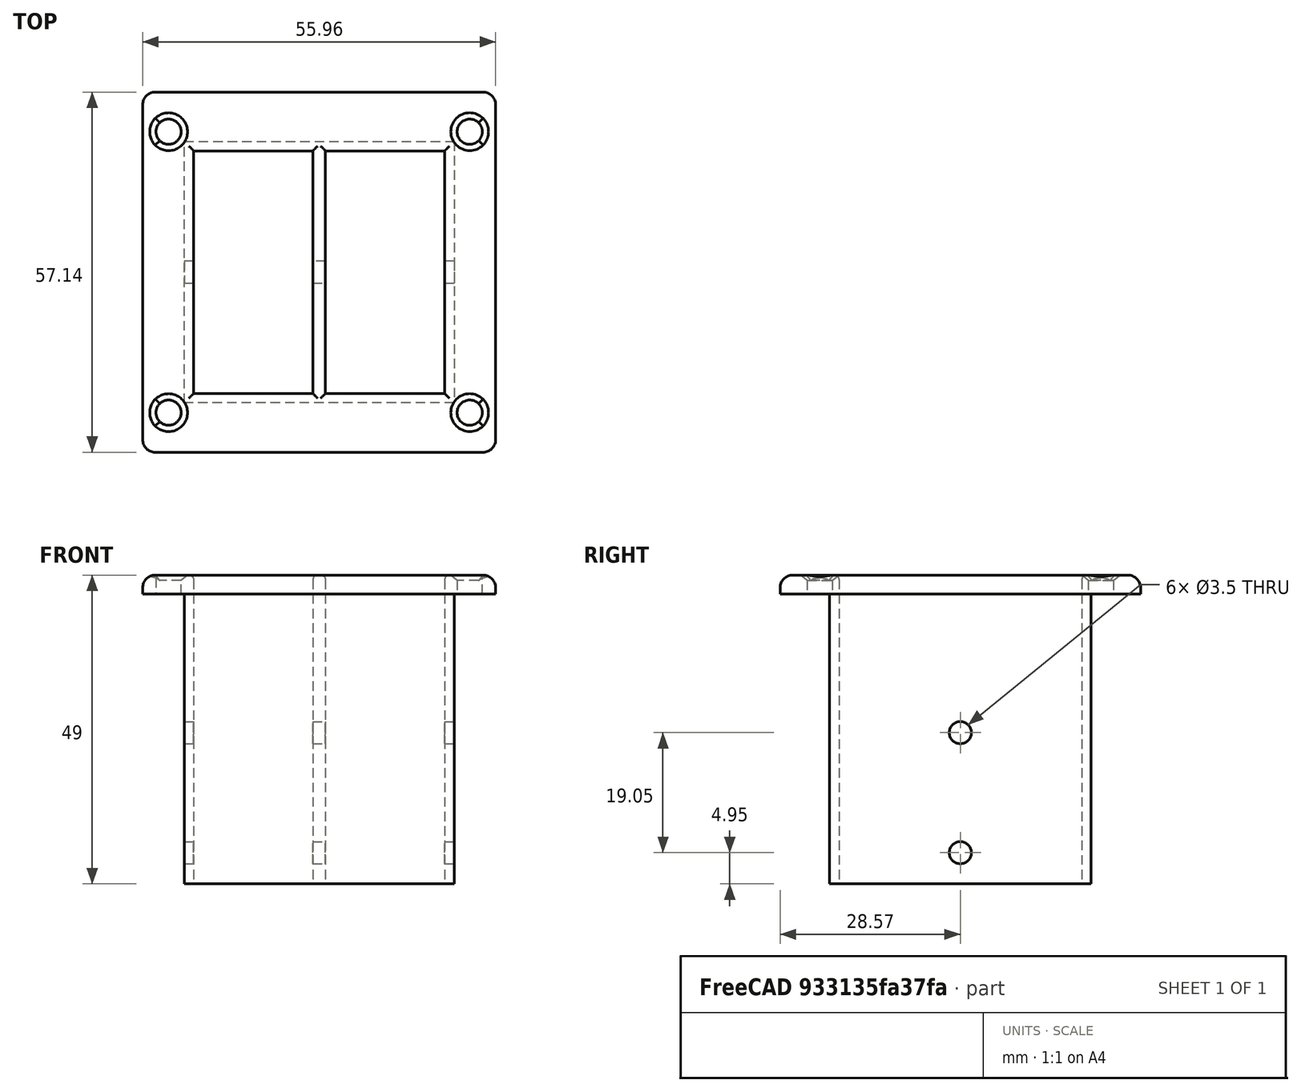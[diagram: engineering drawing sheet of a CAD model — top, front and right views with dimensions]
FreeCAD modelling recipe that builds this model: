
FCSTD DOCUMENT  (FreeCAD 0.19R24291 (Git))
Label: PanelPlate_SB
License: All rights reserved
LicenseURL: http://en.wikipedia.org/wiki/All_rights_reserved
objects: TechDraw::DrawViewDimension×33, Sketcher::SketchObject×10, TechDraw::DrawProjGroupItem×8, PartDesign::Fillet×7, PartDesign::Pocket×6, PartDesign::Pad×4, Spreadsheet::Sheet×2, TechDraw::DrawSVGTemplate×2, PartDesign::Chamfer×2, PartDesign::Body×2, TechDraw::DrawProjGroup×2, TechDraw::DrawPage×2, App::Part×2
note: 50 computed .brp shape members not serialized (recipe doc carries the construction recipe); baked Part::Feature solids carry a one-line shape summary decoded from their .brp

FEATURE [Sketcher::SketchObject] Sketch
  FullyConstrained = true
  MapMode = 5
  Support = -> [XY_Plane001]
  expr: Constraints[10] = <<Spreadsheet_PanelPlate_SB>>.SB1_FacePlateHeight
  expr: Constraints[9] = <<Spreadsheet_PanelPlate_SB>>.SB1_FacePlateWidth
  sketch-geometry (4):
    g0: LineSegment StartX=-19.05 StartY=28.575 StartZ=0 EndX=19.05 EndY=28.575 EndZ=0
    g1: LineSegment StartX=19.05 StartY=28.575 StartZ=0 EndX=19.05 EndY=-28.575 EndZ=0
    g2: LineSegment StartX=19.05 StartY=-28.575 StartZ=0 EndX=-19.05 EndY=-28.575 EndZ=0
    g3: LineSegment StartX=-19.05 StartY=-28.575 StartZ=0 EndX=-19.05 EndY=28.575 EndZ=0
  constraints (11):
    c: Coincident(g0,g1)
    c: Coincident(g1,g2)
    c: Coincident(g2,g3)
    c: Coincident(g3,g0)
    c: Horizontal(g0)
    c: Horizontal(g2)
    c: Vertical(g1)
    c: Vertical(g3)
    c: Symmetric(g0,g1,g-1)
    c: DistanceX(g0,g0) = 38.1
    c: DistanceY(g1,g1) = 57.15
FEATURE [Spreadsheet::Sheet] Spreadsheet  label="Spreadsheet_PanelPlate_SB"
  cells = A1=Panel Plate SB connector; C1=AndersonDept; D1(AndersonDept)==49mm; E1=Given; F1=Anderson_Screw_Ofset; G1(Anderson_Screw_Ofset)==23mm; A2=Based on Powerwerx; C2=AndersonWidth; D2(AndersonWidth)==15.9mm; E2=Given; F2=Anderson_Screw_Space; G2(Anderson_Screw_Space)==25.4 * 0.75mm; A3=Anderson is 37x15.9x49 mm; C3=AndersonHeight; D3(AndersonHeight)==37mm; E3=Given; F3=Anderson_Screw_Hole; G3(Anderson_Screw_Hole)==3.5mm; H3=Measured; A7=One up Panel Plate; D7=Inch; F7=Two up Panel Plate; A8=SB1_FacePlateWidth; B8(SB1_FacePlateWidth)==D8; C8=Guestamet from photo; D8==1.5in; F8=SB2_FacePlateWidth; G8(SB2_FacePlateWidth)==G9 * 2.914 / 2.976; A9=SB1_FacePlateHeight; B9(SB1_FacePlateHeight)==D9; C9=Guestamet from photo; D9==2.25in; F9=SB2_FacePlateHeight; G9(SB2_FacePlateHeight)==B9; A10=SB1_MtgHole_Width; B10(SB1_MtgHole_Width)==D10; C10=From Powerwerx; D10==1.02in; F10=SB2_MtgHole_Width; G10(SB2_MtgHole_Width)==1.88in; A11=SB1_MtgHole_Height; B11(SB1_MtgHole_Height)==D11; C11=From Powerwerx; D11==1.755in; F11=SB2_MtgHole_Height; G11(SB2_MtgHole_Height)==B11; A12=SB1_MtgHole_Diameter; B12(SB1_MtgHole_Diameter)==4mm; C12=Standardizing; F12=SB2_MtgHole_Diameter; G12(SB2_MtgHole_Diameter)==B12; A13=SB1_Thickness; B13(SB1_Thickness)==3mm; C13=Guess; F13=SB2_Thickness; G13(SB2_Thickness)==B13; A15=SB1_ExtrusionWidth; B15(SB1_ExtrusionWidth)==D2 + 2 * E15; D15=Add 2.5mm to Anderson; E15==2.25mm; F15=SB2_ExtrusionWidth; G15(SB2_ExtrusionWidth)==B15 + B15 + G19; H15=wrong; A16=SB1_ExtrusionHeight; B16(SB1_ExtrusionHeight)==D3 + 2 * E15; F16=SB2_ExtrusionHeight; G16(SB2_ExtrusionHeight)==B16; A17=SB1_ExtrusionDepth; B17(SB1_ExtrusionDepth)==D1; F17=SB2_ExtrusionDepth; G17(SB2_ExtrusionDepth)==B17; A18=SB1_ExtrusionWallThick; B18(SB1_ExtrusionWallThick)==1.5mm; F18=SB2_ExtrusionWallThick; G18(SB2_ExtrusionWallThick)==B18; F19=SB2_ExtrusionDividerThick; G19(SB2_ExtrusionDividerThick)==2mm; H19=guess
FEATURE [PartDesign::Pad] Pad  label="PadFaceplateSB1"
  Direction = (1,1,1)
  Length = 3
  Length2 = 100
  Profile = -> Sketch
  Type = 0
  expr: Length = <<Spreadsheet_PanelPlate_SB>>.SB1_Thickness
FEATURE [Sketcher::SketchObject] Sketch001
  FullyConstrained = true
  MapMode = 5
  Support = -> [XY_Plane001]
  expr: Constraints[9] = <<Spreadsheet_PanelPlate_SB>>.SB1_MtgHole_Height
  expr: Constraints[8] = <<Spreadsheet_PanelPlate_SB>>.SB1_MtgHole_Width
  expr: Constraints[0] = <<Spreadsheet_PanelPlate_SB>>.SB1_MtgHole_Diameter
  sketch-geometry (4):
    g0: Circle CenterX=-12.954 CenterY=22.2885 CenterZ=0 NormalX=0 NormalY=0 NormalZ=1 AngleXU=0 Radius=2
    g1: Circle CenterX=-12.954 CenterY=-22.2885 CenterZ=0 NormalX=0 NormalY=0 NormalZ=1 AngleXU=0 Radius=2
    g2: Circle CenterX=12.954 CenterY=22.2885 CenterZ=0 NormalX=0 NormalY=0 NormalZ=1 AngleXU=0 Radius=2
    g3: Circle CenterX=12.954 CenterY=-22.2885 CenterZ=0 NormalX=0 NormalY=0 NormalZ=1 AngleXU=0 Radius=2
  constraints (11):
    c: Diameter(g0) = 4
    c: Equal(g0,g2)
    c: Equal(g2,g3)
    c: Equal(g3,g1)
    c: Horizontal(g0,g2)
    c: Horizontal(g1,g3)
    c: Vertical(g0,g1)
    c: Vertical(g2,g3)
    c: DistanceX(g0,g2) = 25.908
    c: DistanceY(g3,g2) = 44.577
    c: Symmetric(g0,g3,g-1)
FEATURE [PartDesign::Pocket] Pocket  label="PocketMtgHolesSB1"
  BaseFeature = -> Pad
  Length = 5
  Length2 = 100
  Profile = -> Sketch001
  Reversed = true
  Type = 1
FEATURE [Sketcher::SketchObject] Sketch002
  AttachmentOffset = pos=(0,0,3) rot=(0,0,1;0rad)
  FullyConstrained = true
  MapMode = 5
  Placement = pos=(0,0,3) rot=(0,0,1;0rad)
  Support = -> [XY_Plane001]
  expr: Constraints[10] = <<Spreadsheet_PanelPlate_SB>>.SB1_ExtrusionHeight
  expr: Constraints[20] = Spreadsheet.AndersonWidth
  expr: Constraints[21] = <<Spreadsheet_PanelPlate_SB>>.AndersonHeight
  expr: Constraints[9] = <<Spreadsheet_PanelPlate_SB>>.SB1_ExtrusionWidth
  expr: .AttachmentOffset.Base.z = <<Spreadsheet_PanelPlate_SB>>.SB1_Thickness
  sketch-geometry (8):
    g0: LineSegment StartX=-10.2 StartY=20.75 StartZ=0 EndX=10.2 EndY=20.75 EndZ=0
    g1: LineSegment StartX=10.2 StartY=20.75 StartZ=0 EndX=10.2 EndY=-20.75 EndZ=0
    g2: LineSegment StartX=10.2 StartY=-20.75 StartZ=0 EndX=-10.2 EndY=-20.75 EndZ=0
    g3: LineSegment StartX=-10.2 StartY=-20.75 StartZ=0 EndX=-10.2 EndY=20.75 EndZ=0
    g4: LineSegment StartX=-7.95 StartY=18.5 StartZ=0 EndX=7.95 EndY=18.5 EndZ=0
    g5: LineSegment StartX=7.95 StartY=18.5 StartZ=0 EndX=7.95 EndY=-18.5 EndZ=0
    g6: LineSegment StartX=7.95 StartY=-18.5 StartZ=0 EndX=-7.95 EndY=-18.5 EndZ=0
    g7: LineSegment StartX=-7.95 StartY=-18.5 StartZ=0 EndX=-7.95 EndY=18.5 EndZ=0
  constraints (22):
    c: Coincident(g0,g1)
    c: Coincident(g1,g2)
    c: Coincident(g2,g3)
    c: Coincident(g3,g0)
    c: Horizontal(g0)
    c: Horizontal(g2)
    c: Vertical(g1)
    c: Vertical(g3)
    c: Symmetric(g0,g1,g-1)
    c: DistanceX(g0,g0) = 20.4
    c: DistanceY(g3,g3) = 41.5
    c: Coincident(g4,g5)
    c: Coincident(g5,g6)
    c: Coincident(g6,g7)
    c: Coincident(g7,g4)
    c: Horizontal(g4)
    c: Horizontal(g6)
    c: Vertical(g5)
    c: Vertical(g7)
    c: Symmetric(g4,g5,g-1)
    c: DistanceX(g4,g4) = 15.9
    c: DistanceY(g5,g5) = 37
FEATURE [PartDesign::Pad] Pad001  label="PadExtrusionBodyDownSB1"
  BaseFeature = -> Pocket
  Direction = (1,1,1)
  Length = 49
  Length2 = 100
  Profile = -> Sketch002
  Refine = true
  Reversed = true
  Type = 0
  expr: Length = <<Spreadsheet_PanelPlate_SB>>.SB1_ExtrusionDepth
FEATURE [Sketcher::SketchObject] Sketch003
  FullyConstrained = true
  MapMode = 5
  Placement = pos=(0,0,3) rot=(0,0,1;0rad)
  Support = -> [Pad001]
  expr: Constraints[9] = <<Spreadsheet_PanelPlate_SB>>.SB1_ExtrusionHeight - 2 * Spreadsheet.SB1_ExtrusionWallThick
  expr: Constraints[10] = <<Spreadsheet_PanelPlate_SB>>.SB1_ExtrusionWidth - 2 * Spreadsheet.SB1_ExtrusionWallThick
  expr: Constraints[20] = <<Spreadsheet_PanelPlate_SB>>.AndersonWidth
  expr: Constraints[21] = <<Spreadsheet_PanelPlate_SB>>.AndersonHeight
  sketch-geometry (8):
    g0: LineSegment StartX=-8.7 StartY=19.25 StartZ=0 EndX=8.7 EndY=19.25 EndZ=0
    g1: LineSegment StartX=8.7 StartY=19.25 StartZ=0 EndX=8.7 EndY=-19.25 EndZ=0
    g2: LineSegment StartX=8.7 StartY=-19.25 StartZ=0 EndX=-8.7 EndY=-19.25 EndZ=0
    g3: LineSegment StartX=-8.7 StartY=-19.25 StartZ=0 EndX=-8.7 EndY=19.25 EndZ=0
    g4: LineSegment StartX=-7.95 StartY=18.5 StartZ=0 EndX=7.95 EndY=18.5 EndZ=0
    g5: LineSegment StartX=7.95 StartY=18.5 StartZ=0 EndX=7.95 EndY=-18.5 EndZ=0
    g6: LineSegment StartX=7.95 StartY=-18.5 StartZ=0 EndX=-7.95 EndY=-18.5 EndZ=0
    g7: LineSegment StartX=-7.95 StartY=-18.5 StartZ=0 EndX=-7.95 EndY=18.5 EndZ=0
  constraints (22):
    c: Coincident(g0,g1)
    c: Coincident(g1,g2)
    c: Coincident(g2,g3)
    c: Coincident(g3,g0)
    c: Horizontal(g0)
    c: Horizontal(g2)
    c: Vertical(g1)
    c: Vertical(g3)
    c: Symmetric(g0,g1,g-1)
    c: DistanceY(g1,g1) = 38.5
    c: DistanceX(g0,g0) = 17.4
    c: Coincident(g4,g5)
    c: Coincident(g5,g6)
    c: Coincident(g6,g7)
    c: Coincident(g7,g4)
    c: Horizontal(g4)
    c: Horizontal(g6)
    c: Vertical(g5)
    c: Vertical(g7)
    c: Symmetric(g4,g5,g-1)
    c: DistanceX(g4,g4) = 15.9
    c: DistanceY(g5,g5) = 37
FEATURE [TechDraw::DrawSVGTemplate] Template
  EditableTexts = Approved1=Approved 1; Approved2=Approved 2; CheckedBy=20230810; Code=Code; CompanyAddress=publicinvention.org; CompanyName=Public Invention; DrawingNumber=Drawing Number; DrawingTitle1=PanelPlate SB1; DrawingTitle2=For Anderson SB50 Connectors; DrawingTitle3=Drawing Title 3; DrawnBy=(Forrest) Lee Erickson; Revision=Rev; Scale=Scale; Sheet=Sheet 1 of 1
  Height = 215.9
  Orientation = 1
  Width = 279.4
FEATURE [PartDesign::Pocket] Pocket001  label="PocketThroughBodySB1"
  BaseFeature = -> Pad001
  Length = 5
  Length2 = 100
  Profile = -> Sketch003
  Type = 1
FEATURE [Sketcher::SketchObject] Sketch004
  FullyConstrained = true
  MapMode = 5
  Placement = pos=(10.2,0,0) rot=(0.57735,0.57735,0.57735;2.0944rad)
  Support = -> [Pocket001]
  expr: Constraints[2] = <<Spreadsheet_PanelPlate_SB>>.Anderson_Screw_Hole
  expr: Constraints[5] = <<Spreadsheet_PanelPlate_SB>>.Anderson_Screw_Space
  expr: Constraints[4] = Spreadsheet.Anderson_Screw_Ofset - <<Spreadsheet_PanelPlate_SB>>.SB1_Thickness
  sketch-geometry (2):
    g0: Circle CenterX=0 CenterY=-20 CenterZ=0 NormalX=0 NormalY=0 NormalZ=1 AngleXU=0 Radius=1.75
    g1: Circle CenterX=0 CenterY=-39.05 CenterZ=0 NormalX=0 NormalY=0 NormalZ=1 AngleXU=0 Radius=1.75
  constraints (6):
    c: PointOnObject(g0,g-2)
    c: PointOnObject(g1,g-2)
    c: Diameter(g0) = 3.5
    c: Equal(g0,g1)
    c: DistanceY(g0,g-1) = 20
    c: DistanceY(g1,g0) = 19.05
FEATURE [PartDesign::Pocket] Pocket002  label="PocketMoutScrewsSB1"
  BaseFeature = -> Pocket001
  Length = 5
  Length2 = 100
  Profile = -> Sketch004
  Type = 1
FEATURE [PartDesign::Chamfer] Chamfer
  Angle = 41
  Base = -> Pocket002 [Edge28,Edge23,Edge21,Edge22]
  BaseFeature = -> Pocket002
  ChamferType = 2
  FlipDirection = false
  Size = 1
  Size2 = 1
  SupportTransform = false
FEATURE [PartDesign::Fillet] Fillet
  Base = -> Chamfer [Edge20,Edge16,Edge18,Edge15]
  BaseFeature = -> Chamfer
  Radius = 2
  SupportTransform = false
FEATURE [PartDesign::Fillet] Fillet001
  Base = -> Fillet [Edge4,Edge1,Edge5,Edge8]
  BaseFeature = -> Fillet
  Radius = 2
  SupportTransform = false
FEATURE [PartDesign::Fillet] Fillet002
  Base = -> Fillet001 [Edge35,Edge36,Edge28,Edge31,Edge69,Edge67,Edge68,Edge70]
  BaseFeature = -> Fillet001
  Radius = 1
  SupportTransform = false
  expr: Radius = 1mm
FEATURE [PartDesign::Body] Body  label="BodySB1"
  Group = -> [Sketch,Pad,Sketch001,Pocket,Sketch002,Pad001,Sketch003,Pocket001,Sketch004,Pocket002,Chamfer,Fillet,Fillet001,Fillet002]
  Origin = -> Origin001
  Tip = -> Fillet002
FEATURE [TechDraw::DrawProjGroupItem] ProjItem  label="Front"
  CoarseView = false
  Direction = (0,0,1)
  Focus = 100
  HardHidden = false
  IsoCount = 0
  IsoHidden = false
  IsoVisible = false
  LockPosition = true
  Perspective = false
  Rotation = 0
  RotationVector = (1,0,0)
  ScaleType = 2
  SeamHidden = false
  SeamVisible = true
  SmoothHidden = false
  SmoothVisible = true
  Source = -> [Body]
  Type = 0
  X = 0
  XDirection = (1,0,0)
  Y = 0
FEATURE [TechDraw::DrawProjGroupItem] ProjItem001  label="FrontTopRight"
  CoarseView = false
  Direction = (0.57735,0.57735,0.57735)
  Focus = 100
  HardHidden = false
  IsoCount = 0
  IsoHidden = false
  IsoVisible = false
  LockPosition = true
  Perspective = false
  Rotation = 0
  RotationVector = (1,0,0)
  ScaleType = 2
  SeamHidden = false
  SeamVisible = true
  SmoothHidden = false
  SmoothVisible = true
  Source = -> [Body]
  Type = 7
  X = -0.946913
  XDirection = (0.707107,0,-0.707107)
  Y = -85.5036
FEATURE [TechDraw::DrawProjGroupItem] ProjItem003  label="Rear"
  CoarseView = false
  Direction = (0,0,-1)
  Focus = 100
  HardHidden = false
  IsoCount = 0
  IsoHidden = false
  IsoVisible = false
  LockPosition = true
  Perspective = false
  Rotation = 0
  RotationVector = (1,0,0)
  ScaleType = 2
  SeamHidden = false
  SeamVisible = true
  SmoothHidden = false
  SmoothVisible = true
  Source = -> [Body]
  Type = 3
  X = 162.829
  XDirection = (-1,0,0)
  Y = 0
FEATURE [TechDraw::DrawProjGroupItem] ProjItem004  label="Left"
  CoarseView = false
  Direction = (-1,0,1e-16)
  Focus = 100
  HardHidden = false
  IsoCount = 0
  IsoHidden = false
  IsoVisible = false
  LockPosition = true
  Perspective = false
  Rotation = 0
  RotationVector = (1,0,0)
  ScaleType = 2
  SeamHidden = false
  SeamVisible = true
  SmoothHidden = false
  SmoothVisible = true
  Source = -> [Body]
  Type = 1
  X = 75.6096
  XDirection = (1e-16,0,1)
  Y = 0
FEATURE [TechDraw::DrawProjGroup] ProjGroup
  Anchor = -> ProjItem
  AutoDistribute = true
  LockPosition = false
  ProjectionType = 0
  Rotation = 0
  ScaleType = 2
  Source = -> [Body]
  Views = -> [ProjItem,ProjItem001,ProjItem003,ProjItem004]
  X = 70.3259
  Y = 152.806
  spacingX = 15
  spacingY = 15
FEATURE [TechDraw::DrawViewDimension] Dimension001
  Arbitrary = false
  ArbitraryTolerances = false
  EqualTolerance = true
  FormatSpec = %.3f
  FormatSpecOverTolerance = %+.3f
  FormatSpecUnderTolerance = %+.3f
  Inverted = false
  LockPosition = false
  MeasureType = 1
  OverTolerance = 0
  References2D = -> [ProjItem]
  Rotation = 0
  ScaleType = 2
  TheoreticalExact = false
  Type = 2
  UnderTolerance = 0
  X = -31.2615
  Y = -1.58298
FEATURE [TechDraw::DrawViewDimension] Dimension002
  Arbitrary = false
  ArbitraryTolerances = false
  EqualTolerance = true
  FormatSpec = %.3f
  FormatSpecOverTolerance = %+.3f
  FormatSpecUnderTolerance = %+.3f
  Inverted = false
  LockPosition = false
  MeasureType = 1
  OverTolerance = 0
  References2D = -> [ProjItem]
  Rotation = 0
  ScaleType = 2
  TheoreticalExact = false
  Type = 1
  UnderTolerance = 0
  X = -0.452279
  Y = 43.2741
FEATURE [TechDraw::DrawViewDimension] Dimension008
  Arbitrary = false
  ArbitraryTolerances = false
  EqualTolerance = true
  FormatSpec = ⌀%.3f
  FormatSpecOverTolerance = %+.3f
  FormatSpecUnderTolerance = %+.3f
  Inverted = false
  LockPosition = false
  MeasureType = 1
  OverTolerance = 0
  References2D = -> [ProjItem004]
  Rotation = 0
  ScaleType = 2
  TheoreticalExact = false
  Type = 5
  UnderTolerance = 0
  X = -10.4024
  Y = 13.5684
FEATURE [TechDraw::DrawViewDimension] Dimension009
  Arbitrary = false
  ArbitraryTolerances = false
  EqualTolerance = true
  FormatSpec = %.3f
  FormatSpecOverTolerance = %+.3f
  FormatSpecUnderTolerance = %+.3f
  Inverted = false
  LockPosition = false
  MeasureType = 1
  OverTolerance = 0
  References2D = -> [ProjItem003]
  Rotation = 0
  ScaleType = 2
  TheoreticalExact = false
  Type = 2
  UnderTolerance = 0
  X = -37.2431
  Y = -2.68367
FEATURE [TechDraw::DrawViewDimension] Dimension011
  Arbitrary = false
  ArbitraryTolerances = false
  EqualTolerance = true
  FormatSpec = ⌀%.3f
  FormatSpecOverTolerance = %+.3f
  FormatSpecUnderTolerance = %+.3f
  Inverted = false
  LockPosition = false
  MeasureType = 1
  OverTolerance = 0
  References2D = -> [ProjItem]
  Rotation = 0
  ScaleType = 2
  TheoreticalExact = false
  Type = 5
  UnderTolerance = 0
  X = -36.2312
  Y = 39.8067
FEATURE [TechDraw::DrawViewDimension] Dimension012
  Arbitrary = false
  ArbitraryTolerances = false
  EqualTolerance = true
  FormatSpec = %.3f
  FormatSpecOverTolerance = %+.3f
  FormatSpecUnderTolerance = %+.3f
  Inverted = false
  LockPosition = false
  MeasureType = 1
  OverTolerance = 0
  References2D = -> [ProjItem004]
  Rotation = 0
  ScaleType = 2
  TheoreticalExact = false
  Type = 1
  UnderTolerance = 0
  X = -8.74009
  Y = 44.8123
FEATURE [TechDraw::DrawViewDimension] Dimension013
  Arbitrary = false
  ArbitraryTolerances = false
  EqualTolerance = true
  FormatSpec = %.3f
  FormatSpecOverTolerance = %+.3f
  FormatSpecUnderTolerance = %+.3f
  Inverted = false
  LockPosition = false
  MeasureType = 1
  OverTolerance = 0
  References2D = -> [ProjItem004]
  Rotation = 0
  ScaleType = 2
  TheoreticalExact = false
  Type = 1
  UnderTolerance = 0
  X = 10.5465
  Y = 35.6937
FEATURE [TechDraw::DrawViewDimension] Dimension014
  Arbitrary = false
  ArbitraryTolerances = false
  EqualTolerance = true
  FormatSpec = %.3f
  FormatSpecOverTolerance = %+.3f
  FormatSpecUnderTolerance = %+.3f
  Inverted = false
  LockPosition = false
  MeasureType = 1
  OverTolerance = 0
  References2D = -> [ProjItem004]
  Rotation = 0
  ScaleType = 2
  TheoreticalExact = false
  Type = 1
  UnderTolerance = 0
  X = 25.3925
  Y = -34.8696
FEATURE [TechDraw::DrawViewDimension] Dimension015
  Arbitrary = false
  ArbitraryTolerances = false
  EqualTolerance = true
  FormatSpec = %.3f
  FormatSpecOverTolerance = %+.3f
  FormatSpecUnderTolerance = %+.3f
  Inverted = false
  LockPosition = false
  MeasureType = 1
  OverTolerance = 0
  References2D = -> [ProjItem003]
  Rotation = 0
  ScaleType = 2
  TheoreticalExact = false
  Type = 1
  UnderTolerance = 0
  X = 7.86091
  Y = 39.8636
FEATURE [TechDraw::DrawViewDimension] Dimension016
  Arbitrary = false
  ArbitraryTolerances = false
  EqualTolerance = true
  FormatSpec = %.3f
  FormatSpecOverTolerance = %+.3f
  FormatSpecUnderTolerance = %+.3f
  Inverted = false
  LockPosition = false
  MeasureType = 1
  OverTolerance = 0
  References2D = -> [ProjItem004]
  Rotation = 0
  ScaleType = 2
  TheoreticalExact = false
  Type = 1
  UnderTolerance = 0
  X = -1.34889
  Y = -25.9921
FEATURE [TechDraw::DrawViewDimension] Dimension017
  Arbitrary = false
  ArbitraryTolerances = false
  EqualTolerance = true
  FormatSpec = %.3f
  FormatSpecOverTolerance = %+.3f
  FormatSpecUnderTolerance = %+.3f
  Inverted = false
  LockPosition = false
  MeasureType = 1
  OverTolerance = 0
  References2D = -> [ProjItem004]
  Rotation = 0
  ScaleType = 2
  TheoreticalExact = false
  Type = 2
  UnderTolerance = 0
  X = -38.9936
  Y = -2.38363
FEATURE [Sketcher::SketchObject] Sketch007
  AttachmentOffset = pos=(0,0,3) rot=(0,0,1;0rad)
  FullyConstrained = true
  MapMode = 5
  Placement = pos=(0,0,3) rot=(0,0,1;0rad)
  Support = -> [XY_Plane003]
  expr: .AttachmentOffset.Base.z = <<Spreadsheet_PanelPlate_SB>>.SB1_Thickness
  expr: Constraints[9] = <<Spreadsheet_PanelPlate_SB>>.SB2_ExtrusionWidth
  expr: Constraints[21] = <<Spreadsheet_PanelPlate_SB>>.AndersonHeight
  expr: Constraints[20] = Spreadsheet.AndersonWidth
  expr: Constraints[10] = <<Spreadsheet_PanelPlate_SB>>.SB2_ExtrusionHeight
  sketch-geometry (8):
    g0: LineSegment StartX=-21.4 StartY=20.75 StartZ=0 EndX=21.4 EndY=20.75 EndZ=0
    g1: LineSegment StartX=21.4 StartY=20.75 StartZ=0 EndX=21.4 EndY=-20.75 EndZ=0
    g2: LineSegment StartX=21.4 StartY=-20.75 StartZ=0 EndX=-21.4 EndY=-20.75 EndZ=0
    g3: LineSegment StartX=-21.4 StartY=-20.75 StartZ=0 EndX=-21.4 EndY=20.75 EndZ=0
    g4: LineSegment StartX=-7.95 StartY=18.5 StartZ=0 EndX=7.95 EndY=18.5 EndZ=0
    g5: LineSegment StartX=7.95 StartY=18.5 StartZ=0 EndX=7.95 EndY=-18.5 EndZ=0
    g6: LineSegment StartX=7.95 StartY=-18.5 StartZ=0 EndX=-7.95 EndY=-18.5 EndZ=0
    g7: LineSegment StartX=-7.95 StartY=-18.5 StartZ=0 EndX=-7.95 EndY=18.5 EndZ=0
  constraints (22):
    c: Coincident(g0,g1)
    c: Coincident(g1,g2)
    c: Coincident(g2,g3)
    c: Coincident(g3,g0)
    c: Horizontal(g0)
    c: Horizontal(g2)
    c: Vertical(g1)
    c: Vertical(g3)
    c: Symmetric(g0,g1,g-1)
    c: DistanceX(g0,g0) = 42.8
    c: DistanceY(g3,g3) = 41.5
    c: Coincident(g4,g5)
    c: Coincident(g5,g6)
    c: Coincident(g6,g7)
    c: Coincident(g7,g4)
    c: Horizontal(g4)
    c: Horizontal(g6)
    c: Vertical(g5)
    c: Vertical(g7)
    c: Symmetric(g4,g5,g-1)
    c: DistanceX(g4,g4) = 15.9
    c: DistanceY(g5,g5) = 37
FEATURE [Sketcher::SketchObject] Sketch008
  FullyConstrained = true
  MapMode = 5
  Support = -> [XY_Plane003]
  expr: Constraints[0] = <<Spreadsheet_PanelPlate_SB>>.SB1_MtgHole_Diameter
  expr: Constraints[8] = <<Spreadsheet_PanelPlate_SB>>.SB2_MtgHole_Width
  expr: Constraints[9] = <<Spreadsheet_PanelPlate_SB>>.SB2_MtgHole_Height
  sketch-geometry (4):
    g0: Circle CenterX=-23.876 CenterY=22.2885 CenterZ=0 NormalX=0 NormalY=0 NormalZ=1 AngleXU=0 Radius=2
    g1: Circle CenterX=-23.876 CenterY=-22.2885 CenterZ=0 NormalX=0 NormalY=0 NormalZ=1 AngleXU=0 Radius=2
    g2: Circle CenterX=23.876 CenterY=22.2885 CenterZ=0 NormalX=0 NormalY=0 NormalZ=1 AngleXU=0 Radius=2
    g3: Circle CenterX=23.876 CenterY=-22.2885 CenterZ=0 NormalX=0 NormalY=0 NormalZ=1 AngleXU=0 Radius=2
  constraints (11):
    c: Diameter(g0) = 4
    c: Equal(g0,g2)
    c: Equal(g2,g3)
    c: Equal(g3,g1)
    c: Horizontal(g0,g2)
    c: Horizontal(g1,g3)
    c: Vertical(g0,g1)
    c: Vertical(g2,g3)
    c: DistanceX(g0,g2) = 47.752
    c: DistanceY(g3,g2) = 44.577
    c: Symmetric(g0,g3,g-1)
FEATURE [Sketcher::SketchObject] Sketch009
  FullyConstrained = true
  MapMode = 5
  Support = -> [XY_Plane003]
  expr: Constraints[9] = <<Spreadsheet_PanelPlate_SB>>.SB2_FacePlateWidth
  expr: Constraints[10] = <<Spreadsheet_PanelPlate_SB>>.SB2_FacePlateHeight
  sketch-geometry (4):
    g0: LineSegment StartX=-27.9797 StartY=28.575 StartZ=0 EndX=27.9797 EndY=28.575 EndZ=0
    g1: LineSegment StartX=27.9797 StartY=28.575 StartZ=0 EndX=27.9797 EndY=-28.575 EndZ=0
    g2: LineSegment StartX=27.9797 StartY=-28.575 StartZ=0 EndX=-27.9797 EndY=-28.575 EndZ=0
    g3: LineSegment StartX=-27.9797 StartY=-28.575 StartZ=0 EndX=-27.9797 EndY=28.575 EndZ=0
  constraints (11):
    c: Coincident(g0,g1)
    c: Coincident(g1,g2)
    c: Coincident(g2,g3)
    c: Coincident(g3,g0)
    c: Horizontal(g0)
    c: Horizontal(g2)
    c: Vertical(g1)
    c: Vertical(g3)
    c: Symmetric(g0,g1,g-1)
    c: DistanceX(g0,g0) = 55.9594
    c: DistanceY(g1,g1) = 57.15
FEATURE [PartDesign::Pad] Pad003  label="PadFaceplateSB002"
  Direction = (1,1,1)
  Length = 3
  Length2 = 100
  Profile = -> Sketch009
  Type = 0
  expr: Length = <<Spreadsheet_PanelPlate_SB>>.SB1_Thickness
FEATURE [PartDesign::Pocket] Pocket005  label="PocketMtgHolesSB002"
  BaseFeature = -> Pad003
  Length = 5
  Length2 = 100
  Profile = -> Sketch008
  Reversed = true
  Type = 1
FEATURE [PartDesign::Pad] Pad002  label="PadExtrusionBodyDownSB002"
  BaseFeature = -> Pocket005
  Direction = (1,1,1)
  Length = 49
  Length2 = 100
  Profile = -> Sketch007
  Refine = true
  Reversed = true
  Type = 0
  expr: Length = <<Spreadsheet_PanelPlate_SB>>.SB1_ExtrusionDepth
FEATURE [Sketcher::SketchObject] Sketch005
  FullyConstrained = true
  MapMode = 5
  Placement = pos=(0,0,3) rot=(0,0,1;0rad)
  Support = -> [Pad002]
  expr: Constraints[30] = <<Spreadsheet_PanelPlate_SB2>>.SB2_ExtrusionDividerThick
  expr: Constraints[9] = <<Spreadsheet_PanelPlate_SB>>.SB2_ExtrusionHeight - 2 * Spreadsheet.SB2_ExtrusionWallThick
  expr: Constraints[27] = <<Spreadsheet_PanelPlate_SB>>.AndersonHeight + 5mm
  expr: Constraints[26] = <<Spreadsheet_PanelPlate_SB>>.AndersonWidth
  expr: Constraints[10] = <<Spreadsheet_PanelPlate_SB>>.SB2_ExtrusionWidth - 2 * Spreadsheet.SB2_ExtrusionWallThick
  sketch-geometry (16):
    g0: LineSegment StartX=-19.9 StartY=19.25 StartZ=0 EndX=-1 EndY=19.25 EndZ=0
    g1: LineSegment StartX=19.9 StartY=19.25 StartZ=0 EndX=19.9 EndY=-19.25 EndZ=0
    g2: LineSegment StartX=19.9 StartY=-19.25 StartZ=0 EndX=1 EndY=-19.25 EndZ=0
    g3: LineSegment StartX=-19.9 StartY=-19.25 StartZ=0 EndX=-19.9 EndY=19.25 EndZ=0
    g4: LineSegment StartX=-16.9 StartY=21 StartZ=0 EndX=-1 EndY=21 EndZ=0
    g5: LineSegment StartX=-1 StartY=21 StartZ=0 EndX=-1 EndY=-21 EndZ=0
    g6: LineSegment StartX=-1 StartY=-21 StartZ=0 EndX=-16.9 EndY=-21 EndZ=0
    g7: LineSegment StartX=-16.9 StartY=-21 StartZ=0 EndX=-16.9 EndY=21 EndZ=0
    g8: LineSegment StartX=1 StartY=21 StartZ=0 EndX=16.9 EndY=21 EndZ=0
    g9: LineSegment StartX=16.9 StartY=21 StartZ=0 EndX=16.9 EndY=-21 EndZ=0
    g10: LineSegment StartX=16.9 StartY=-21 StartZ=0 EndX=1 EndY=-21 EndZ=0
    g11: LineSegment StartX=1 StartY=-21 StartZ=0 EndX=1 EndY=21 EndZ=0
    g12: LineSegment StartX=1 StartY=19.25 StartZ=0 EndX=1 EndY=-19.25 EndZ=0
    g13: LineSegment StartX=-1 StartY=-19.25 StartZ=0 EndX=-1 EndY=19.25 EndZ=0
    g14: LineSegment StartX=1 StartY=19.25 StartZ=0 EndX=19.9 EndY=19.25 EndZ=0
    g15: LineSegment StartX=-1 StartY=-19.25 StartZ=0 EndX=-19.9 EndY=-19.25 EndZ=0
  constraints (44):
    c: Coincident(g14,g1)
    c: Coincident(g1,g2)
    c: Coincident(g15,g3)
    c: Coincident(g3,g0)
    c: Horizontal(g0)
    c: Horizontal(g2)
    c: Vertical(g1)
    c: Vertical(g3)
    c: Symmetric(g0,g1,g-1)
    c: DistanceY(g1,g1) = 38.5
    c: DistanceX(g0,g14) = 39.8
    c: Coincident(g4,g5)
    c: Coincident(g5,g6)
    c: Coincident(g6,g7)
    c: Coincident(g7,g4)
    c: Horizontal(g4)
    c: Horizontal(g6)
    c: Vertical(g5)
    c: Coincident(g8,g9)
    c: Coincident(g9,g10)
    c: Coincident(g10,g11)
    c: Coincident(g11,g8)
    c: Horizontal(g8)
    c: Horizontal(g10)
    c: Vertical(g9)
    c: Vertical(g11)
    c: DistanceX(g4,g4) = 15.9
    c: DistanceY(g5,g5) = 42
    c: Equal(g5,g11)
    c: Equal(g4,g8)
    c: DistanceX(g4,g8) = 2
    c: Symmetric(g4,g6,g-1)
    c: Symmetric(g4,g8,g-2)
    c: PointOnObject(g12,g11)
    c: PointOnObject(g12,g11)
    c: PointOnObject(g13,g5)
    c: PointOnObject(g13,g0)
    c: Vertical(g13)
    c: PointOnObject(g0,g5)
    c: Tangent(g0,g14)
    c: Tangent(g2,g15)
    c: Coincident(g12,g14)
    c: Coincident(g2,g12)
    c: Coincident(g13,g15)
FEATURE [PartDesign::Pocket] Pocket003  label="PocketThroughBodySB002"
  BaseFeature = -> Pad002
  Length = 5
  Length2 = 100
  Profile = -> Sketch005
  Type = 1
FEATURE [Spreadsheet::Sheet] Spreadsheet001  label="Spreadsheet_PanelPlate_SB2"
  cells = A1=Panel Plate SB connector; C1=AndersonDept; D1(AndersonDept)==49mm; E1=Given; F1=Anderson_Screw_Ofset; G1(Anderson_Screw_Ofset)==23mm; A2=Based on Powerwerx; C2=AndersonWidth; D2(AndersonWidth)==15.9mm; E2=Given; F2=Anderson_Screw_Space; G2(Anderson_Screw_Space)==25.4 * 0.75mm; A3=Anderson is 37x15.9x49 mm; C3=AndersonHeight; D3(AndersonHeight)==37mm; E3=Given; F3=Anderson_Screw_Hole; G3(Anderson_Screw_Hole)==3.5mm; H3=Measured; A7=One up Panel Plate; D7=Inch; F7=Two up Panel Plate; A8=SB1_FacePlateWidth; B8(SB1_FacePlateWidth)==D8; C8=Guestamet from photo; D8==1.5in; F8=SB2_FacePlateWidth; G8(SB2_FacePlateWidth)==G9 * 2.914 / 2.976; A9=SB1_FacePlateHeight; B9(SB1_FacePlateHeight)==D9; C9=Guestamet from photo; D9==2.25in; F9=SB2_FacePlateHeight; G9(SB2_FacePlateHeight)==B9; A10=SB1_MtgHole_Width; B10(SB1_MtgHole_Width)==D10; C10=From Powerwerx; D10==1.02in; F10=SB2_MtgHole_Width; G10(SB2_MtgHole_Width)==1.88in; A11=SB1_MtgHole_Height; B11(SB1_MtgHole_Height)==D11; C11=From Powerwerx; D11==1.755in; F11=SB2_MtgHole_Height; G11(SB2_MtgHole_Height)==B11; A12=SB1_MtgHole_Diameter; B12(SB1_MtgHole_Diameter)==4mm; C12=Standardizing; F12=SB2_MtgHole_Diameter; G12(SB2_MtgHole_Diameter)==B12; A13=SB1_Thickness; B13(SB1_Thickness)==3mm; C13=Guess; F13=SB2_Thickness; G13(SB2_Thickness)==B13; A15=SB1_ExtrusionWidth; B15(SB1_ExtrusionWidth)==D2 + 2 * E15; D15=Add 2.5mm to Anderson; E15==2.25mm; F15=SB2_ExtrusionWidth; G15(SB2_ExtrusionWidth)==B15 + B15 + G19; H15=wrong; A16=SB1_ExtrusionHeight; B16(SB1_ExtrusionHeight)==D3 + 2 * E15; F16=SB2_ExtrusionHeight; G16(SB2_ExtrusionHeight)==B16; A17=SB1_ExtrusionDepth; B17(SB1_ExtrusionDepth)==D1; F17=SB2_ExtrusionDepth; G17(SB2_ExtrusionDepth)==B17; A18=SB1_ExtrusionWallThick; B18(SB1_ExtrusionWallThick)==1.5mm; F18=SB2_ExtrusionWallThick; G18(SB2_ExtrusionWallThick)==B18; F19=SB2_ExtrusionDividerThick; G19(SB2_ExtrusionDividerThick)==2mm; H19=guess
FEATURE [Sketcher::SketchObject] Sketch015
  FullyConstrained = true
  MapMode = 5
  Placement = pos=(0,0,0) rot=(0.57735,0.57735,0.57735;2.0944rad)
  Support = -> [YZ_Plane003]
  expr: Constraints[5] = <<Spreadsheet_PanelPlate_SB2>>.Anderson_Screw_Space
  expr: Constraints[4] = <<Spreadsheet_PanelPlate_SB2>>.Anderson_Screw_Ofset - 1mm
  expr: Constraints[0] = <<Spreadsheet_PanelPlate_SB2>>.Anderson_Screw_Hole
  sketch-geometry (2):
    g0: Circle CenterX=0 CenterY=-22 CenterZ=0 NormalX=0 NormalY=0 NormalZ=1 AngleXU=0 Radius=1.75
    g1: Circle CenterX=0 CenterY=-41.05 CenterZ=0 NormalX=0 NormalY=0 NormalZ=1 AngleXU=0 Radius=1.75
  constraints (6):
    c: Diameter(g0) = 3.5
    c: Equal(g0,g1)
    c: Vertical(g-1,g0)
    c: Vertical(g0,g1)
    c: DistanceY(g0,g-1) = 22
    c: DistanceY(g1,g0) = 19.05
FEATURE [PartDesign::Pocket] Pocket008  label="PocketMountScrewsSB2"
  BaseFeature = -> Pocket003
  Length = 5
  Length2 = 100
  Midplane = true
  Profile = -> Sketch015
  Type = 1
FEATURE [TechDraw::DrawSVGTemplate] Template001
  EditableTexts = Approved1=Approved 1; Approved2=Approved 2; CheckedBy=20230810; Code=Code; CompanyAddress=publicinvention.org; CompanyName=Public Invention; DrawingNumber=Drawing Number; DrawingTitle1=PanelPlate SB2; DrawingTitle2=For Anderson SB50 Connectors; DrawingTitle3=Drawing Title 3; DrawnBy=(Forrest) Lee Erickson; Revision=Rev; Scale=Scale; Sheet=Sheet 1 of 1
  Height = 215.9
  Orientation = 1
  Width = 279.4
FEATURE [PartDesign::Fillet] Fillet003
  Base = -> Pocket008 [Edge1,Edge2,Edge5,Edge8]
  BaseFeature = -> Pocket008
  Radius = 2
  SupportTransform = false
FEATURE [PartDesign::Fillet] Fillet004
  Base = -> Fillet003 [Edge24,Edge4,Edge25,Edge28]
  BaseFeature = -> Fillet003
  Radius = 2
  SupportTransform = false
FEATURE [PartDesign::Chamfer] Chamfer001
  Angle = 41
  Base = -> Fillet004 [Edge35,Edge34,Edge40,Edge45]
  BaseFeature = -> Fillet004
  ChamferType = 2
  FlipDirection = false
  Size = 1
  Size2 = 1
  SupportTransform = false
FEATURE [PartDesign::Fillet] Fillet005
  Base = -> Chamfer001 [Edge21,Edge22,Edge20,Edge19]
  BaseFeature = -> Chamfer001
  Radius = 0.75
  SupportTransform = false
FEATURE [PartDesign::Fillet] Fillet006
  Base = -> Fillet005 [Edge21,Edge20,Edge19,Edge22]
  BaseFeature = -> Fillet005
  Radius = 0.75
  SupportTransform = false
FEATURE [PartDesign::Body] Body001  label="BodySB2"
  Group = -> [Sketch009,Pad003,Sketch008,Pocket005,Sketch007,Pad002,Sketch005,Pocket003,Sketch015,Pocket008,Fillet003,Fillet004,Chamfer001,Fillet005,Fillet006]
  Origin = -> Origin003
  Tip = -> Fillet006
FEATURE [TechDraw::DrawProjGroupItem] ProjItem005  label="Front001"
  CoarseView = false
  Direction = (0,0,1)
  Focus = 100
  HardHidden = false
  IsoCount = 0
  IsoHidden = false
  IsoVisible = false
  LockPosition = true
  Perspective = false
  Rotation = 0
  RotationVector = (1,0,0)
  ScaleType = 2
  SeamHidden = false
  SeamVisible = true
  SmoothHidden = false
  SmoothVisible = true
  Source = -> [Body001]
  Type = 0
  X = 0
  XDirection = (1,0,0)
  Y = 0
FEATURE [TechDraw::DrawProjGroupItem] ProjItem006  label="FrontTopRight001"
  CoarseView = false
  Direction = (0.57735,0.57735,0.57735)
  Focus = 100
  HardHidden = false
  IsoCount = 0
  IsoHidden = false
  IsoVisible = false
  LockPosition = true
  Perspective = false
  Rotation = 0
  RotationVector = (1,0,0)
  ScaleType = 2
  SeamHidden = false
  SeamVisible = true
  SmoothHidden = false
  SmoothVisible = true
  Source = -> [Body001]
  Type = 7
  X = 2.00567
  XDirection = (0.707107,0,-0.707107)
  Y = -88.0462
FEATURE [TechDraw::DrawProjGroupItem] ProjItem007  label="Left001"
  CoarseView = false
  Direction = (-1,0,1e-16)
  Focus = 100
  HardHidden = false
  IsoCount = 0
  IsoHidden = false
  IsoVisible = false
  LockPosition = true
  Perspective = false
  Rotation = 0
  RotationVector = (1,0,0)
  ScaleType = 2
  SeamHidden = false
  SeamVisible = true
  SmoothHidden = false
  SmoothVisible = true
  Source = -> [Body001]
  Type = 1
  X = 93.845
  XDirection = (1e-16,0,1)
  Y = 0
FEATURE [TechDraw::DrawProjGroupItem] ProjItem008  label="Rear001"
  CoarseView = false
  Direction = (0,0,-1)
  Focus = 100
  HardHidden = false
  IsoCount = 0
  IsoHidden = false
  IsoVisible = false
  LockPosition = true
  Perspective = false
  Rotation = 0
  RotationVector = (1,0,0)
  ScaleType = 2
  SeamHidden = false
  SeamVisible = true
  SmoothHidden = false
  SmoothVisible = true
  Source = -> [Body001]
  Type = 3
  X = 157.811
  XDirection = (-1,0,0)
  Y = 0
FEATURE [TechDraw::DrawProjGroup] ProjGroup001
  Anchor = -> ProjItem005
  AutoDistribute = true
  LockPosition = false
  ProjectionType = 0
  Rotation = 0
  ScaleType = 2
  Source = -> [Body001]
  Views = -> [ProjItem005,ProjItem006,ProjItem007,ProjItem008]
  X = 65.56
  Y = 154.196
  spacingX = 15
  spacingY = 15
FEATURE [TechDraw::DrawViewDimension] Dimension018
  Arbitrary = false
  ArbitraryTolerances = false
  EqualTolerance = true
  FormatSpec = %.3f
  FormatSpecOverTolerance = %+.3f
  FormatSpecUnderTolerance = %+.3f
  Inverted = false
  LockPosition = false
  MeasureType = 1
  OverTolerance = 0
  References2D = -> [ProjItem005]
  Rotation = 0
  ScaleType = 2
  TheoreticalExact = false
  Type = 1
  UnderTolerance = 0
  X = 1.6553
  Y = 40.4795
FEATURE [TechDraw::DrawViewDimension] Dimension019
  Arbitrary = false
  ArbitraryTolerances = false
  EqualTolerance = true
  FormatSpec = %.3f
  FormatSpecOverTolerance = %+.3f
  FormatSpecUnderTolerance = %+.3f
  Inverted = false
  LockPosition = false
  MeasureType = 1
  OverTolerance = 0
  References2D = -> [ProjItem005]
  Rotation = 0
  ScaleType = 2
  TheoreticalExact = false
  Type = 2
  UnderTolerance = 0
  X = 48.3263
  Y = 0.33106
FEATURE [TechDraw::DrawViewDimension] Dimension020
  Arbitrary = false
  ArbitraryTolerances = false
  EqualTolerance = true
  FormatSpec = ⌀%.3f
  FormatSpecOverTolerance = %+.3f
  FormatSpecUnderTolerance = %+.3f
  Inverted = false
  LockPosition = false
  MeasureType = 1
  OverTolerance = 0
  References2D = -> [ProjItem005]
  Rotation = 0
  ScaleType = 2
  TheoreticalExact = false
  Type = 5
  UnderTolerance = 0
  X = -40.925
  Y = 38.7213
FEATURE [TechDraw::DrawViewDimension] Dimension021
  Arbitrary = false
  ArbitraryTolerances = false
  EqualTolerance = true
  FormatSpec = ⌀%.3f
  FormatSpecOverTolerance = %+.3f
  FormatSpecUnderTolerance = %+.3f
  Inverted = false
  LockPosition = false
  MeasureType = 1
  OverTolerance = 0
  References2D = -> [ProjItem005]
  Rotation = 0
  ScaleType = 2
  TheoreticalExact = false
  Type = 5
  UnderTolerance = 0
  X = -42.8999
  Y = -35.1751
FEATURE [TechDraw::DrawViewDimension] Dimension022
  Arbitrary = false
  ArbitraryTolerances = false
  EqualTolerance = true
  FormatSpec = %.3f
  FormatSpecOverTolerance = %+.3f
  FormatSpecUnderTolerance = %+.3f
  Inverted = false
  LockPosition = false
  MeasureType = 1
  OverTolerance = 0
  References2D = -> [ProjItem007]
  Rotation = 0
  ScaleType = 2
  TheoreticalExact = false
  Type = 2
  UnderTolerance = 0
  X = -35.3974
  Y = -1.24148
FEATURE [TechDraw::DrawViewDimension] Dimension023
  Arbitrary = false
  ArbitraryTolerances = false
  EqualTolerance = true
  FormatSpec = %.3f
  FormatSpecOverTolerance = %+.3f
  FormatSpecUnderTolerance = %+.3f
  Inverted = false
  LockPosition = false
  MeasureType = 1
  OverTolerance = 0
  References2D = -> [ProjItem007]
  Rotation = 0
  ScaleType = 2
  TheoreticalExact = false
  Type = 1
  UnderTolerance = 0
  X = -2.90276
  Y = -25.567
FEATURE [TechDraw::DrawViewDimension] Dimension024
  Arbitrary = false
  ArbitraryTolerances = false
  EqualTolerance = true
  FormatSpec = %.3f
  FormatSpecOverTolerance = %+.3f
  FormatSpecUnderTolerance = %+.3f
  Inverted = false
  LockPosition = false
  MeasureType = 1
  OverTolerance = 0
  References2D = -> [ProjItem007]
  Rotation = 0
  ScaleType = 2
  TheoreticalExact = false
  Type = 1
  UnderTolerance = 0
  X = 5.07878
  Y = -32.2578
FEATURE [TechDraw::DrawViewDimension] Dimension025
  Arbitrary = false
  ArbitraryTolerances = false
  EqualTolerance = true
  FormatSpec = %.3f
  FormatSpecOverTolerance = %+.3f
  FormatSpecUnderTolerance = %+.3f
  Inverted = false
  LockPosition = false
  MeasureType = 1
  OverTolerance = 0
  References2D = -> [ProjItem008]
  Rotation = 0
  ScaleType = 2
  TheoreticalExact = false
  Type = 1
  UnderTolerance = 0
  X = 12.9346
  Y = -32.0102
FEATURE [TechDraw::DrawViewDimension] Dimension026
  Arbitrary = false
  ArbitraryTolerances = false
  EqualTolerance = true
  FormatSpec = %.3f
  FormatSpecOverTolerance = %+.3f
  FormatSpecUnderTolerance = %+.3f
  Inverted = false
  LockPosition = false
  MeasureType = 1
  OverTolerance = 0
  References2D = -> [ProjItem008]
  Rotation = 0
  ScaleType = 2
  TheoreticalExact = false
  Type = 1
  UnderTolerance = 0
  X = 21.0638
  Y = 38.4842
FEATURE [TechDraw::DrawViewDimension] Dimension027
  Arbitrary = false
  ArbitraryTolerances = false
  EqualTolerance = true
  FormatSpec = %.3f
  FormatSpecOverTolerance = %+.3f
  FormatSpecUnderTolerance = %+.3f
  Inverted = false
  LockPosition = false
  MeasureType = 1
  OverTolerance = 0
  References2D = -> [ProjItem008]
  Rotation = 0
  ScaleType = 2
  TheoreticalExact = false
  Type = 2
  UnderTolerance = 0
  X = 26.4436
  Y = -20.5518
FEATURE [TechDraw::DrawViewDimension] Dimension028
  Arbitrary = false
  ArbitraryTolerances = false
  EqualTolerance = true
  FormatSpec = %.3f
  FormatSpecOverTolerance = %+.3f
  FormatSpecUnderTolerance = %+.3f
  Inverted = false
  LockPosition = false
  MeasureType = 1
  OverTolerance = 0
  References2D = -> [ProjItem005]
  Rotation = 0
  ScaleType = 2
  TheoreticalExact = false
  Type = 1
  UnderTolerance = 0
  X = -0.125923
  Y = -38.1548
FEATURE [TechDraw::DrawViewDimension] Dimension029
  Arbitrary = false
  ArbitraryTolerances = false
  EqualTolerance = true
  FormatSpec = %.3f
  FormatSpecOverTolerance = %+.3f
  FormatSpecUnderTolerance = %+.3f
  Inverted = false
  LockPosition = false
  MeasureType = 1
  OverTolerance = 0
  References2D = -> [ProjItem005]
  Rotation = 0
  ScaleType = 2
  TheoreticalExact = false
  Type = 2
  UnderTolerance = 0
  X = 31.3055
  Y = -1.13331
FEATURE [TechDraw::DrawViewDimension] Dimension030
  Arbitrary = false
  ArbitraryTolerances = false
  EqualTolerance = true
  FormatSpec = %.3f
  FormatSpecOverTolerance = %+.3f
  FormatSpecUnderTolerance = %+.3f
  Inverted = false
  LockPosition = false
  MeasureType = 1
  OverTolerance = 0
  References2D = -> [ProjItem008]
  Rotation = 0
  ScaleType = 2
  TheoreticalExact = false
  Type = 1
  UnderTolerance = 0
  X = -14.2156
  Y = 41.8337
FEATURE [TechDraw::DrawViewDimension] Dimension031
  Arbitrary = false
  ArbitraryTolerances = false
  EqualTolerance = true
  FormatSpec = %.3f
  FormatSpecOverTolerance = %+.3f
  FormatSpecUnderTolerance = %+.3f
  Inverted = false
  LockPosition = false
  MeasureType = 1
  OverTolerance = 0
  References2D = -> [ProjItem008]
  Rotation = 0
  ScaleType = 2
  TheoreticalExact = false
  Type = 2
  UnderTolerance = 0
  X = 7.9625
  Y = 0.453323
FEATURE [TechDraw::DrawViewDimension] Dimension032
  Arbitrary = false
  ArbitraryTolerances = false
  EqualTolerance = true
  FormatSpec = %.3f
  FormatSpecOverTolerance = %+.3f
  FormatSpecUnderTolerance = %+.3f
  Inverted = false
  LockPosition = false
  MeasureType = 1
  OverTolerance = 0
  References2D = -> [ProjItem007]
  Rotation = 0
  ScaleType = 2
  TheoreticalExact = false
  Type = 1
  UnderTolerance = 0
  X = 6.56249
  Y = 36.1749
FEATURE [TechDraw::DrawViewDimension] Dimension033
  Arbitrary = false
  ArbitraryTolerances = false
  EqualTolerance = true
  FormatSpec = %.3f
  FormatSpecOverTolerance = %+.3f
  FormatSpecUnderTolerance = %+.3f
  Inverted = false
  LockPosition = false
  MeasureType = 1
  OverTolerance = 0
  References2D = -> [ProjItem007]
  Rotation = 0
  ScaleType = 2
  TheoreticalExact = false
  Type = 1
  UnderTolerance = 0
  X = -10.7299
  Y = 44.6978
FEATURE [TechDraw::DrawPage] Page001  label="PagePanelPlateSB2"
  KeepUpdated = true
  NextBalloonIndex = 1
  ProjectionType = 0
  Template = -> Template001
  Views = -> [ProjGroup001,Dimension018,Dimension019,Dimension020,Dimension021,Dimension022,Dimension023,Dimension024,Dimension025,Dimension026,Dimension027,Dimension028,Dimension029,Dimension030,Dimension031,Dimension032,Dimension033]
FEATURE [App::Part] Part001  label="PartSB2"
  Group = -> [Body001,Page001]
  Origin = -> Origin002
FEATURE [TechDraw::DrawViewDimension] Dimension034
  Arbitrary = false
  ArbitraryTolerances = false
  EqualTolerance = true
  FormatSpec = %.3f
  FormatSpecOverTolerance = %+.3f
  FormatSpecUnderTolerance = %+.3f
  Inverted = false
  LockPosition = false
  MeasureType = 1
  OverTolerance = 0
  References2D = -> [ProjItem]
  Rotation = 0
  ScaleType = 2
  TheoreticalExact = false
  Type = 1
  UnderTolerance = 0
  X = 0.14938
  Y = -36.2232
FEATURE [TechDraw::DrawViewDimension] Dimension035
  Arbitrary = false
  ArbitraryTolerances = false
  EqualTolerance = true
  FormatSpec = %.3f
  FormatSpecOverTolerance = %+.3f
  FormatSpecUnderTolerance = %+.3f
  Inverted = false
  LockPosition = false
  MeasureType = 1
  OverTolerance = 0
  References2D = -> [ProjItem]
  Rotation = 0
  ScaleType = 2
  TheoreticalExact = false
  Type = 2
  UnderTolerance = 0
  X = 20.0526
  Y = 1.07554
FEATURE [TechDraw::DrawViewDimension] Dimension
  Arbitrary = false
  ArbitraryTolerances = false
  EqualTolerance = true
  FormatSpec = ⌀%.3f
  FormatSpecOverTolerance = %+.3f
  FormatSpecUnderTolerance = %+.3f
  Inverted = false
  LockPosition = false
  MeasureType = 1
  OverTolerance = 0
  References2D = -> [ProjItem]
  Rotation = 0
  ScaleType = 2
  TheoreticalExact = false
  Type = 5
  UnderTolerance = 0
  X = -41.0013
  Y = -36.2885
FEATURE [TechDraw::DrawViewDimension] Dimension036
  Arbitrary = false
  ArbitraryTolerances = false
  EqualTolerance = true
  FormatSpec = %.3f
  FormatSpecOverTolerance = %+.3f
  FormatSpecUnderTolerance = %+.3f
  Inverted = false
  LockPosition = false
  MeasureType = 1
  OverTolerance = 0
  References2D = -> [ProjItem]
  Rotation = 0
  ScaleType = 2
  TheoreticalExact = false
  Type = 1
  UnderTolerance = 0
  X = -2.35639
  Y = -43.8552
FEATURE [TechDraw::DrawViewDimension] Dimension037
  Arbitrary = false
  ArbitraryTolerances = false
  EqualTolerance = true
  FormatSpec = %.3f
  FormatSpecOverTolerance = %+.3f
  FormatSpecUnderTolerance = %+.3f
  Inverted = false
  LockPosition = false
  MeasureType = 1
  OverTolerance = 0
  References2D = -> [ProjItem]
  Rotation = 0
  ScaleType = 2
  TheoreticalExact = false
  Type = 2
  UnderTolerance = 0
  X = 27.8894
  Y = 1.41384
FEATURE [TechDraw::DrawViewDimension] Dimension038
  Arbitrary = false
  ArbitraryTolerances = false
  EqualTolerance = true
  FormatSpec = %.3f
  FormatSpecOverTolerance = %+.3f
  FormatSpecUnderTolerance = %+.3f
  Inverted = false
  LockPosition = false
  MeasureType = 1
  OverTolerance = 0
  References2D = -> [ProjItem003]
  Rotation = 0
  ScaleType = 2
  TheoreticalExact = false
  Type = 1
  UnderTolerance = 0
  X = -0.954558
  Y = -45.2958
FEATURE [TechDraw::DrawPage] Page  label="PagePanelPlateSB1"
  KeepUpdated = true
  NextBalloonIndex = 1
  ProjectionType = 0
  Template = -> Template
  Views = -> [ProjGroup,Dimension001,Dimension002,Dimension008,Dimension009,Dimension011,Dimension012,Dimension013,Dimension014,Dimension015,Dimension016,Dimension017,Dimension034,Dimension035,Dimension,Dimension036,Dimension037,Dimension038]
FEATURE [App::Part] Part  label="PartSB1"
  Group = -> [Body,Page]
  Origin = -> Origin
